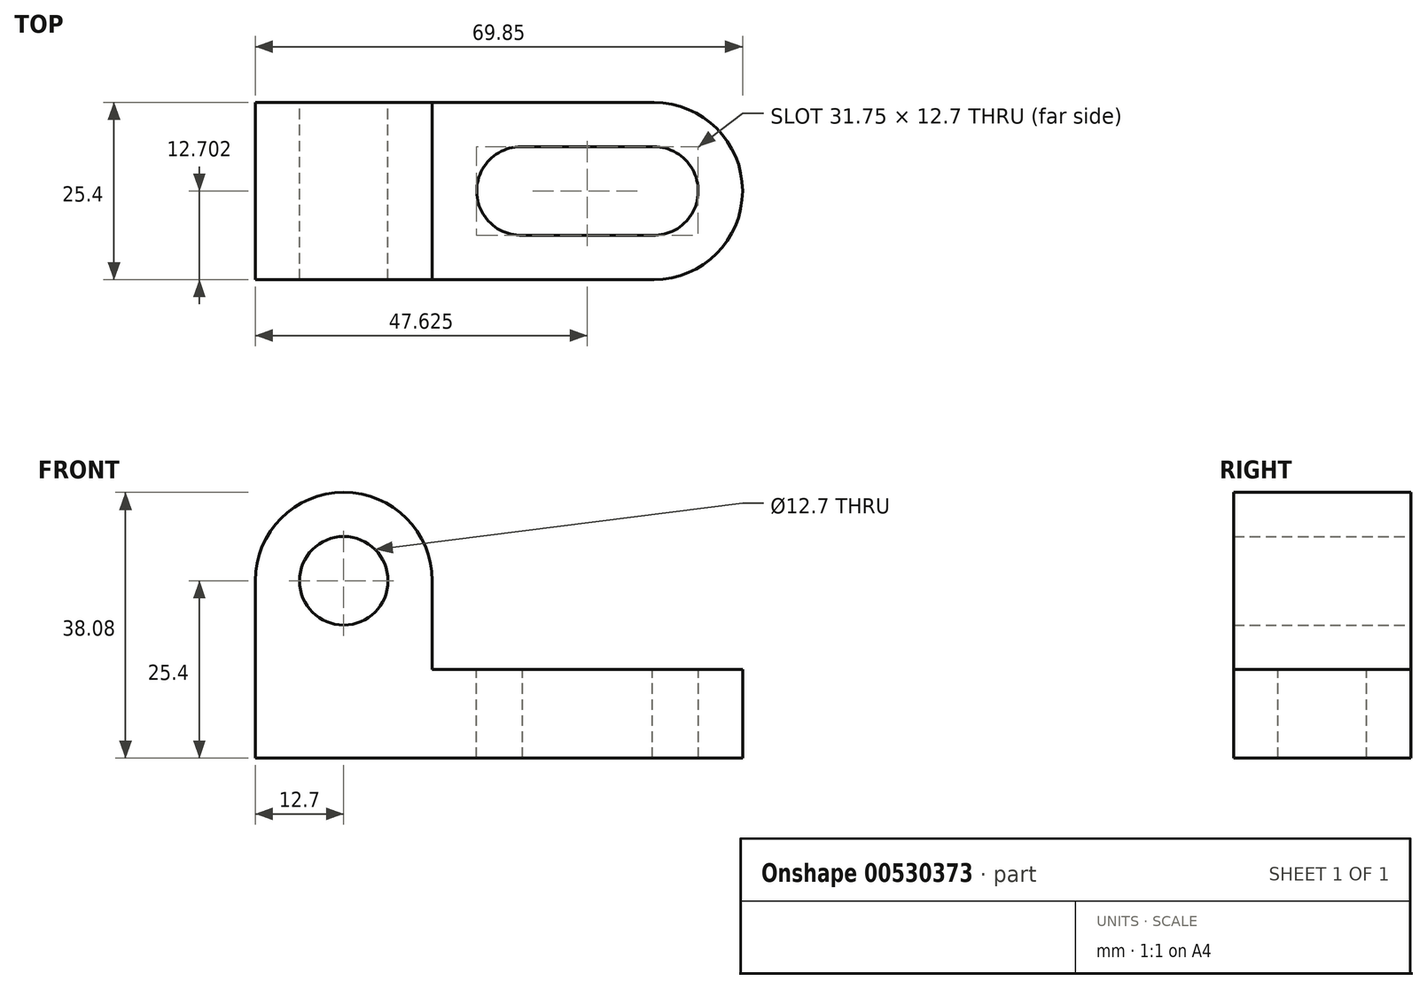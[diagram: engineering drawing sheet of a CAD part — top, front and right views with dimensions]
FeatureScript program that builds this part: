
annotation { "Feature Type Name" : "Feature", "Feature Type Description" : "" }
export const myFeature = defineFeature(function(context is Context, id is Id, definition is map)
    precondition{}
    {
        {
            var Q0;
            Q0=qCreatedBy(makeId("Front.planeOp"),FACE);
            var sketch = newSketch(context, id + "F0", { "sketchPlane" : qUnion([Q0])});
            skLineSegment(sketch, "E0", {"start": v(-69.85, 38.1) * mm, "end": v(-69.85, 0) * mm});
            skLineSegment(sketch, "E1", {"start": v(-69.85, 0) * mm, "end": v(0, 0) * mm});
            skLineSegment(sketch, "E2", {"start": v(0, 0) * mm, "end": v(0, 12.7) * mm});
            skLineSegment(sketch, "E3", {"start": v(0, 12.7) * mm, "end": v(-44.45, 12.7) * mm});
            skLineSegment(sketch, "E4", {"start": v(-44.45, 12.7) * mm, "end": v(-44.45, 38.1) * mm});
            skLineSegment(sketch, "E5", {"start": v(-44.45, 38.1) * mm, "end": v(-69.85, 38.1) * mm});
            skArc(sketch, "E6", {"start": v(-44.45, 25.4) * mm, "mid": v(-57.15, 38.1) * mm, "end": v(-69.85, 25.4) * mm});
            skPoint(sketch, "E6.endSnap0", {"position": v(-44.45, 25.4) * mm});
            skCircle(sketch, "E7", {"center": v(-57.15, 25.4) * mm, "radius": 6.35 * mm});
            skSolve(sketch);
        }
        {
            var Q0;
            Q0 = qSketchRegion(id + "F0", true);
            extrude(context, id + "F1", {"entities" : qUnion([Q0]), "depth" : 25.4 * mm, "offsetDistance" : 25.4 * mm});
        }
        {
            var Q0;
            Q0=makeQuery(id+"F1.opExtrude","CAP_FACE",FACE,{"disambiguationData":[OSD([sQuery(id+"F0.wireOp",EDGE,"E0"),sQuery(id+"F0.wireOp",EDGE,"E1"),sQuery(id+"F0.wireOp",EDGE,"E2"),sQuery(id+"F0.wireOp",EDGE,"E3"),sQuery(id+"F0.wireOp",EDGE,"E4"),sQuery(id+"F0.wireOp",EDGE,"E5"),sQuery(id+"F0.wireOp",EDGE,"E7")])],"isStart":false});
            var sketch = newSketch(context, id + "F2", { "sketchPlane" : qUnion([Q0])});
            skArc(sketch, "E8", {"start": v(-44.45, 25.4) * mm, "mid": v(-57.15, 38.08) * mm, "end": v(-69.85, 25.4) * mm});
            skSolve(sketch);
        }
        {
            var Q0;
            {var subQ0=sQuery(id+"F2.wireOp",EDGE,"E8");Q0=makeQuery(id+"F2.imprint","IMPRINT",FACE,{"disambiguationData":[TD([[makeQuery(id+"F2.imprint","IMPRINT",EDGE,{"derivedFrom":subQ0}),-1.0]])]});}
            extrude(context, id + "F3", {"entities" : qUnion([Q0]), "operationType" : NewBodyOperationType.REMOVE, "endBound" : BoundingType.THROUGH_ALL, "oppositeDirection" : true, "depth" : 25.4 * mm, "offsetDistance" : 25.4 * mm});
        }
        {
            var Q0;
            Q0=makeQuery(id+"F1.opExtrude","SWEPT_FACE",FACE,{"disambiguationData":[OSD([sQuery(id+"F0.wireOp",EDGE,"E3")])]});
            var sketch = newSketch(context, id + "F4", { "sketchPlane" : qUnion([Q0])});
            skArc(sketch, "E9", {"start": v(-12.7, -25.4) * mm, "mid": v(0, -12.7) * mm, "end": v(-12.7, 0) * mm});
            skCircle(sketch, "E10", {"center": v(-31.75, -12.7) * mm, "radius": 6.35 * mm});
            skCircle(sketch, "E11", {"center": v(-12.7, -12.7) * mm, "radius": 6.35 * mm});
            skSolve(sketch);
        }
        {
            var Q0;
            Q0=makeQuery(id+"F4.imprint","IMPRINT",FACE,{"disambiguationData":[TD([[makeQuery(id+"F4.imprint","IMPRINT",EDGE,{"derivedFrom":sQuery(id+"F4.wireOp",EDGE,"E10")}),1.0]])]});
            var Q1;
            Q1=makeQuery(id+"F4.imprint","IMPRINT",FACE,{"disambiguationData":[TD([[makeQuery(id+"F4.imprint","IMPRINT",EDGE,{"derivedFrom":sQuery(id+"F4.wireOp",EDGE,"E11")}),1.0]])]});
            var Q2;
            {var subQ0=sQuery(id+"F4.wireOp",EDGE,"E9");Q2=makeQuery(id+"F4.imprint","IMPRINT",FACE,{"disambiguationData":[TD([[makeQuery(id+"F4.imprint","IMPRINT",EDGE,{"derivedFrom":subQ0}),-1.0]])]});}
            extrude(context, id + "F5", {"entities" : qUnion([Q0, Q1, Q2]), "operationType" : NewBodyOperationType.REMOVE, "endBound" : BoundingType.THROUGH_ALL, "oppositeDirection" : true, "depth" : 25.4 * mm, "offsetDistance" : 25.4 * mm});
        }
        {
            var Q0;
            Q0=makeQuery(id+"F1.opExtrude","SWEPT_FACE",FACE,{"disambiguationData":[OSD([sQuery(id+"F0.wireOp",EDGE,"E3")])]});
            var sketch = newSketch(context, id + "F6", { "sketchPlane" : qUnion([Q0])});
            skLineSegment(sketch, "E12", {"start": v(-31.75, -6.35) * mm, "end": v(-12.7, -6.35) * mm});
            skLineSegment(sketch, "E13", {"start": v(-31.96, -19.05) * mm, "end": v(-12.9, -19.05) * mm});
            skSolve(sketch);
        }
        {
            var Q0;
            {var subQ0=sQuery(id+"F6.wireOp",EDGE,"E12");Q0=makeQuery(id+"F6.imprint","IMPRINT",FACE,{"disambiguationData":[TD([[makeQuery(id+"F6.imprint","IMPRINT",EDGE,{"derivedFrom":subQ0}),-1.0]])]});}
            extrude(context, id + "F7", {"entities" : qUnion([Q0]), "operationType" : NewBodyOperationType.REMOVE, "endBound" : BoundingType.THROUGH_ALL, "oppositeDirection" : true, "depth" : 25.4 * mm, "offsetDistance" : 25.4 * mm});
        }
    });
